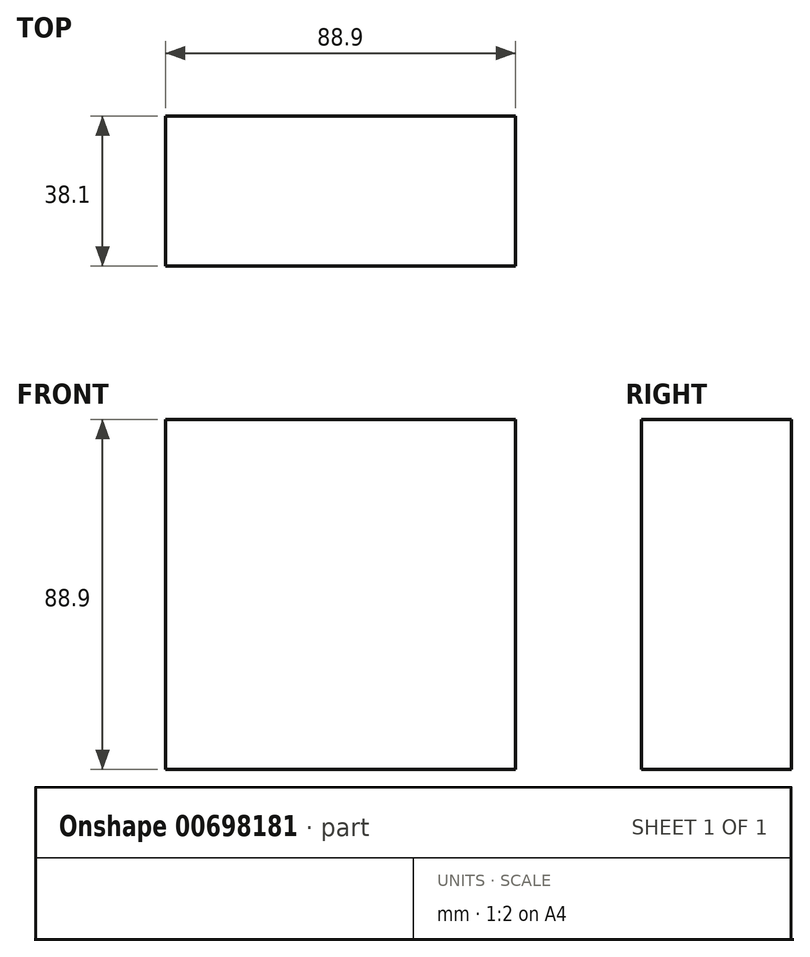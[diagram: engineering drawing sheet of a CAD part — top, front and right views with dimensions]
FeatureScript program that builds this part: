
annotation { "Feature Type Name" : "Feature", "Feature Type Description" : "" }
export const myFeature = defineFeature(function(context is Context, id is Id, definition is map)
    precondition{}
    {
        {
            var Q0;
            Q0=qCreatedBy(makeId("Front.planeOp"),FACE);
            var sketch = newSketch(context, id + "F0", { "sketchPlane" : qUnion([Q0])});
            skLineSegment(sketch, "E0.bottom", {"start": v(-88.9, 0) * mm, "end": v(0, 0) * mm});
            skLineSegment(sketch, "E0.top", {"start": v(-88.9, 88.9) * mm, "end": v(0, 88.9) * mm});
            skLineSegment(sketch, "E0.left", {"start": v(-88.9, 0) * mm, "end": v(-88.9, 88.9) * mm});
            skLineSegment(sketch, "E0.right", {"start": v(0, 0) * mm, "end": v(0, 88.9) * mm});
            skSolve(sketch);
        }
        {
            var Q0;
            Q0 = qSketchRegion(id + "F0", true);
            extrude(context, id + "F1", {"entities" : qUnion([Q0]), "depth" : 38.1 * mm, "offsetDistance" : 25.4 * mm});
        }
    });
